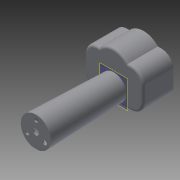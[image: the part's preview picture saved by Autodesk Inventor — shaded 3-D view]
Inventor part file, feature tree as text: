
AUTODESK INVENTOR PART (.ipt)
format: ipt  version: 2014 (Build 180170000, 170)  size: 363,008 bytes
history: native  units: mm
features: sketch x11, extrude x9, fillet x4, other x2, loft x1, shell x1, projected_geometry x1
ambient origin geometry x8: Origin, YZ Plane, XZ Plane, XY Plane, X Axis, Y Axis, Z Axis, Center Point
bodies: Body1 (feature_tree)
feature tree (29):
  other  "ソリッド1"
  sketch  "スケッチ1"
  other  "作業平面1"
  loft  "ロフト1"
  extrude  "押し出し1"  Depth=65.0mm
  shell  "シェル1"  Thickness=21.0mm
  extrude  "押し出し5"  TaperAngle=0.0deg  [1 undecoded]
  extrude  "押し出し9"  TaperAngle=0.0deg  [1 undecoded]
  fillet  "フィレット4"  Radius=8.5mm
  extrude  "押し出し10"  Depth=3.5mm
  extrude  "押し出し14"  Depth=30.0mm TaperAngle=360.0deg
  extrude  "押し出し15"  Depth=1.3mm TaperAngle=0.0deg
  fillet  "フィレット6"  Radius=1.3mm
  extrude  "押し出し11"  Depth=6.0mm
  sketch  "スケッチ16"
  extrude  "押し出し13"  Depth=4.0mm
  fillet  "フィレット8"  Radius=18.5mm
  fillet  "フィレット9"  Radius=3.0mm
  extrude  "押し出し17"  Depth=5.0mm
  sketch  "スケッチ2"
  sketch  "スケッチ3"
  sketch  "スケッチ7"
  sketch  "スケッチ11"
  sketch  "スケッチ12"
  sketch  "スケッチ13"
  sketch  "スケッチ17"
  sketch  "スケッチ18"
  projected_geometry  "投影ループ3"
  sketch  "スケッチ22"
note: 2 required parameter values undecoded (feature->parameter linkage not recoverable at this tier; creation-order binding heuristic only, values carry confidence <= 0.55)
